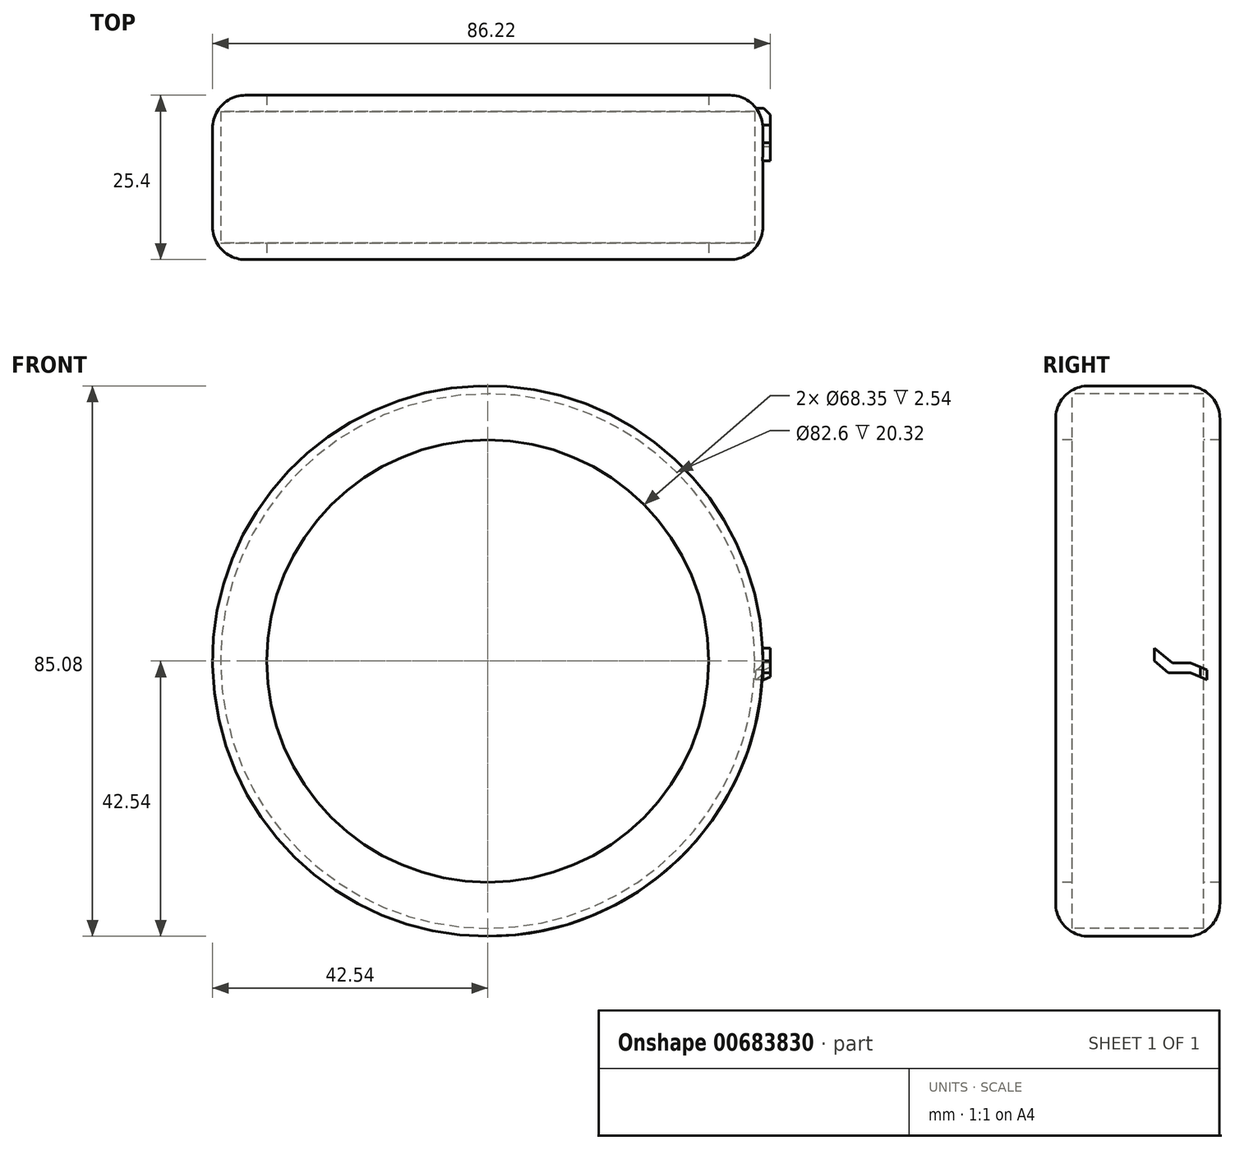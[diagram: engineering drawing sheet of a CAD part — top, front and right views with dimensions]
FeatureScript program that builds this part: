
annotation { "Feature Type Name" : "Feature", "Feature Type Description" : "" }
export const myFeature = defineFeature(function(context is Context, id is Id, definition is map)
    precondition{}
    {
        {
            var Q0;
            Q0=qCreatedBy(makeId("Front.planeOp"),FACE);
            var sketch = newSketch(context, id + "F0", { "sketchPlane" : qUnion([Q0])});
            skCircle(sketch, "E0", {"center": v(0, 0) * mm, "radius": 42.54 * mm});
            skSolve(sketch);
        }
        {
            var Q0;
            Q0=makeQuery(id+"F0.imprint","IMPRINT",FACE,{"disambiguationData":[TD([[makeQuery(id+"F0.imprint","IMPRINT",EDGE,{"derivedFrom":sQuery(id+"F0.wireOp",EDGE,"E0")}),1.0]])]});
            extrude(context, id + "F1", {"entities" : qUnion([Q0]), "depth" : 12.7 * mm, "offsetDistance" : 25.4 * mm, "hasSecondDirection" : true, "secondDirectionOppositeDirection" : true, "secondDirectionDepth" : 12.7 * mm});
        }
        {
            var Q0;
            Q0=makeQuery(id+"F1.opExtrude","SWEPT_FACE",FACE,{"disambiguationData":[OSD([sQuery(id+"F0.wireOp",EDGE,"E0")])]});
            fillet(context, id + "F2", {"entities" : qUnion([Q0]), "radius" : 5.08 * mm, "tangentPropagation" : true, "allowEdgeOverflow" : false});
        }
        {
            var Q0;
            Q0=makeQuery(id+"F1.opExtrude","CAP_FACE",FACE,{"disambiguationData":[OSD([sQuery(id+"F0.wireOp",EDGE,"E0")])],"isStart":false});
            var sketch = newSketch(context, id + "F3", { "sketchPlane" : qUnion([Q0])});
            skCircle(sketch, "E1", {"center": v(0, 0) * mm, "radius": 34.17 * mm});
            skSolve(sketch);
        }
        {
            var Q0;
            Q0=makeQuery(id+"F3.imprint","IMPRINT",FACE,{"disambiguationData":[TD([[makeQuery(id+"F3.imprint","IMPRINT",EDGE,{"derivedFrom":sQuery(id+"F3.wireOp",EDGE,"E1")}),1.0]])]});
            extrude(context, id + "F4", {"entities" : qUnion([Q0]), "operationType" : NewBodyOperationType.REMOVE, "oppositeDirection" : true, "depth" : 86.7 * mm, "offsetDistance" : 25.4 * mm});
        }
        {
            var Q0;
            Q0=makeQuery(id+"F4.boolean.opBoolean","COPY",FACE,{"derivedFrom":makeQuery(id+"F4.opExtrude","SWEPT_FACE",FACE,{"disambiguationData":[OSD([sQuery(id+"F3.wireOp",EDGE,"E1")])]})});
            shell(context, id + "F5", {"entities" : qUnion([Q0]), "thickness" : 2.54 * mm});
        }
        {
            var Q0;
            Q0=qCreatedBy(makeId("Right.planeOp"),FACE);
            var sketch = newSketch(context, id + "F6", { "sketchPlane" : qUnion([Q0])});
            skLineSegment(sketch, "E2.left", {"start": v(2.56, 1.45) * mm, "end": v(2.56, 0) * mm});
            skPoint(sketch, "E3.endSnap0", {"position": v(2.56, 0.43) * mm});
            skPoint(sketch, "E4.orphan", {"position": v(2.56, 1.5) * mm});
            skLineSegment(sketch, "E5", {"start": v(2.56, 1.5) * mm, "end": v(2.56, 2) * mm});
            skLineSegment(sketch, "E6.left", {"start": v(2.56, 2) * mm, "end": v(2.56, 1.45) * mm});
            skLineSegment(sketch, "E6.right", {"start": v(10.7, -1.38) * mm, "end": v(10.7, -2.9) * mm});
            skLineSegment(sketch, "E7.trimOffspring", {"start": v(2.56, 0.43) * mm, "end": v(2.56, 0) * mm});
            skLineSegment(sketch, "E8", {"start": v(2.56, 2) * mm, "end": v(5.34, -0.26) * mm});
            skLineSegment(sketch, "E9", {"start": v(5.34, -0.26) * mm, "end": v(8.12, -0.26) * mm});
            skLineSegment(sketch, "E10", {"start": v(8.12, -0.26) * mm, "end": v(10.7, -1.38) * mm});
            skLineSegment(sketch, "E11", {"start": v(2.56, 0) * mm, "end": v(4.74, -1.78) * mm});
            skLineSegment(sketch, "E12", {"start": v(8.12, -1.78) * mm, "end": v(4.74, -1.78) * mm});
            skLineSegment(sketch, "E13", {"start": v(8.12, -1.78) * mm, "end": v(10.7, -2.9) * mm});
            skSolve(sketch);
        }
        {
            var Q0;
            Q0 = qSketchRegion(id + "F6", true);
            extrude(context, id + "F7", {"entities" : qUnion([Q0]), "operationType" : NewBodyOperationType.ADD, "depth" : 43.68 * mm, "offsetDistance" : 25.4 * mm});
        }
        {
            var Q0;
            Q0=makeQuery(id+"F7.opExtrude","CAP_EDGE",EDGE,{"disambiguationData":[OSD([sQuery(id+"F6.wireOp",EDGE,"E6.right")])],"isStart":false});
            chamfer(context, id + "F8", {"entities" : qUnion([Q0]), "width" : 1.02 * mm, "tangentPropagation" : true});
        }
        {
            var Q0;
            Q0=qCreatedBy(makeId("Front.planeOp"),FACE);
            var sketch = newSketch(context, id + "F9", { "sketchPlane" : qUnion([Q0])});
            skCircle(sketch, "E14", {"center": v(0, 0) * mm, "radius": 34.17 * mm});
            skSolve(sketch);
        }
        {
            var Q0;
            Q0 = qSketchRegion(id + "F9", true);
            extrude(context, id + "F10", {"entities" : qUnion([Q0]), "operationType" : NewBodyOperationType.REMOVE, "oppositeDirection" : true, "depth" : 37.76 * mm, "offsetDistance" : 25.4 * mm, "hasSecondDirection" : true, "secondDirectionOppositeDirection" : false, "secondDirectionDepth" : 25.9 * mm});
        }
        {
            var Q0;
            Q0=qCreatedBy(makeId("Front.planeOp"),FACE);
            var sketch = newSketch(context, id + "F11", { "sketchPlane" : qUnion([Q0])});
            skCircle(sketch, "E15", {"center": v(0, 0) * mm, "radius": 41.3 * mm});
            skSolve(sketch);
        }
        {
            var Q0;
            Q0 = qSketchRegion(id + "F11", true);
            extrude(context, id + "F12", {"entities" : qUnion([Q0]), "operationType" : NewBodyOperationType.REMOVE, "oppositeDirection" : true, "depth" : 10.16 * mm, "offsetDistance" : 25.4 * mm, "hasSecondDirection" : true, "secondDirectionOppositeDirection" : false, "secondDirectionDepth" : 10.16 * mm});
        }
    });
